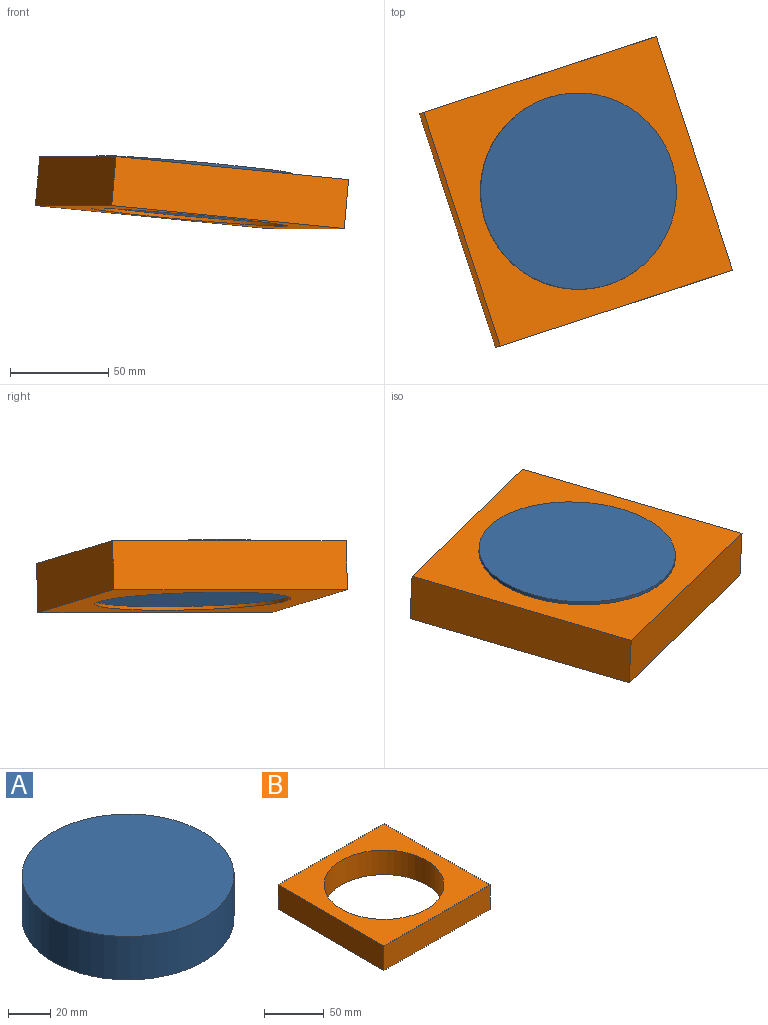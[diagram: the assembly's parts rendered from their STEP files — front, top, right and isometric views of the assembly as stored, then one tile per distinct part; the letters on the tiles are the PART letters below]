
ASSEMBLY  parts=2 mates=1
PART A: 3 faces, bbox 100x100x25 mm
  f0: cylinder r=50mm len=100mm, axis (0,0,-1), area 7854mm2, adj f1,f2
  f1: plane 100x100mm, normal (0,0,1), area 7854mm2, adj f0
  f2: plane 100x100mm, normal (0,0,-1), area 7854mm2, adj f0
PART B: 7 faces, bbox 125x125x25 mm
  f0: plane 125x25mm, normal (1,0,0), area 3125mm2, adj f1,f3,f4,f5
  f1: plane 125x25mm, normal (0,1,0), area 3125mm2, adj f0,f2,f4,f5
  f2: plane 125x25mm, normal (-1,0,0), area 3125mm2, adj f1,f3,f4,f5
  f3: plane 125x25mm, normal (0,-1,0), area 3125mm2, adj f0,f2,f4,f5
  f4: plane 125x125mm, normal (0,0,1), area 7771mm2, adj f0,f1,f2,f3,f6
  f5: plane 125x125mm, normal (0,0,-1), area 7771mm2, adj f0,f1,f2,f3,f6
  f6: cylinder r=50mm len=100mm, axis (0,0,-1), area 7854mm2, adj f4,f5
PLACE A rot(axis=(0.03,0.05,1),108.2deg) t=(26.1,5.79,2.15)mm
PLACE B rot(axis=(0.03,0.05,1),108.2deg) t=(25.94,5.74,0.41)mm
MATE slider A.f0 <-> B.f6  axis (0.09,0.03,1) through (28.33,6.52,27.04)mm
